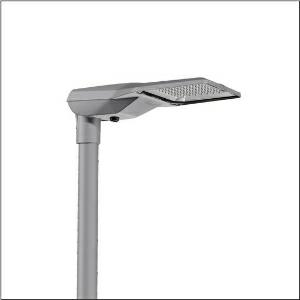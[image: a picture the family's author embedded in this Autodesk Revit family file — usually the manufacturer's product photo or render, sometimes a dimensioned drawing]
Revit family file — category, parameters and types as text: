
# Revit family: streetlight_sl_21_iq_midi___p0_5a_5xe3v31u08nb_f0ed
name_source: partatom
category: Lighting Fixtures
units: mm (PartAtom-declared; Revit-internal decimal feet)

## family parameters
Cut with Voids When Loaded = No
Host = Face
Light Source = No
Part Type = Normal
Room Calculation Point = No
Round Connector Dimension = Use Diameter
Shared = No

## types (1)
- --- (1 x LED, 21180 lm, 136.6 W, 3000K)
    Apparent Load = 137 VA
    CIE Flux Codes = 37 73 96 100 100
    Color Rendering = 70
    Color Temperature = 3000K
    Default Elevation = 1800 mm
    Description = Streetlight SL 21 iQ midi, mast luminaire, primary light control with lens, of PMMA, primary optical cover: cover, of toughened safety glass, transparent, light distribution: P0.5a, light emission: direct distribution, primary light characteristic: asymmetric, installation type: post-top, side-entry, LED, High Power LED, rated luminous flux: 21.180lm, luminous efficacy: 155lm/W, light colour: 730, colour temperature: 3000K, control gear: iQ-Street Remote, D4i with power reduction, control: pre-setting: logarithmic dimming characteristic, Street-Remote, Auto-Match, Temp-Guard, Lumen-Switch, Night-Set, Smart-Wire, Light-Fading, Desk-Remote (wireless, voltage-free reading and setting of iQ features in the workshop via application-optimized NFC function/RFID function), optimised constant luminous flux control (CLO 2.0), mains connection: 230..240V, AC, 50/60Hz, start of lifetime: 137W, end of service life: 144W, reduction: 61W, luminaire housing, of diecast aluminium, powder-coated, Siteco® metallic grey (DB 702S), corrosivity category C5 mid according to DIN EN ISO 12944, please order mast flange separately, inclination adjustable: 0°, 5°, 10°, 15°, sealing non-destructively replaceable, multi-level sealing system, length: 644mm, width: 335mm, height: 110mm, mast flange for spigot size: 42mm (side-entry): 5XC10008XM4, 60/48mm (side-entry/post-top): 5XC10108XM2, 76/60mm (side-entry/post-top): 5XC10108XM1, mounting height: 4..8m, Smart Interface below, protection rating (complete): IP66, insulation class (complete): insulation class II (safety insulation), certification: CE, ENEC, ENEC+, VDE, impact resistance: IK10, permissible operating ambient temperature for outdoor applications: -40..+50°C, standard-compliant lighting for roads and squares, packaging unit: 1 piece

Light Distribution: P0.5a
    Height = 111 mm
    Lamp = 1 x LED
    Lamp Light Flux = 21180 lm
    Lamp Power = 136.6 W
    Lamp count = 1
    Length = 644 mm
    Luminous efficacy = 155 lm/W
    Manufacturer = Siteco
    ModVariant = No
    Model = 5XE3V31U08NB
    Number of Poles = 1
    OnlyDefault = Yes
    Power Factor = 1
    Product Name = Streetlight SL 21 iQ midi | P0.5a
    Product group = mast luminaire | pylon top
    ProductGroupID = 6100
    Protection Class = Protection class II
    Protection Degree = IP 66
    RLX_Detail_Level = 1
    RLX_Emergency_Light_Flux = 0 lm
    RLX_Emergency_Type = 0
    RLX_Emergency_Type_DB = No
    RlxData = <blob elided: 90857 chars, md5=f845605c>
    Socket = socket
    Standby Power = 0 W
    System Light Flux = 21180 lm
    System Power = 137 W
    Type Comments = factory setting: luminous flux: 100 % | dim-lin: 254 | 733 mA
    Type Image = l_1004300.jpg
    URL = http://relux.com
    VarID = @adj_090873
    Voltage = 0 V
    Weight = 0.00 kg
    Width = 336 mm

## geometry (parser evidence)
native form markers: Blend x4, Sweep x12
no freeform markers — native parametric forms only
